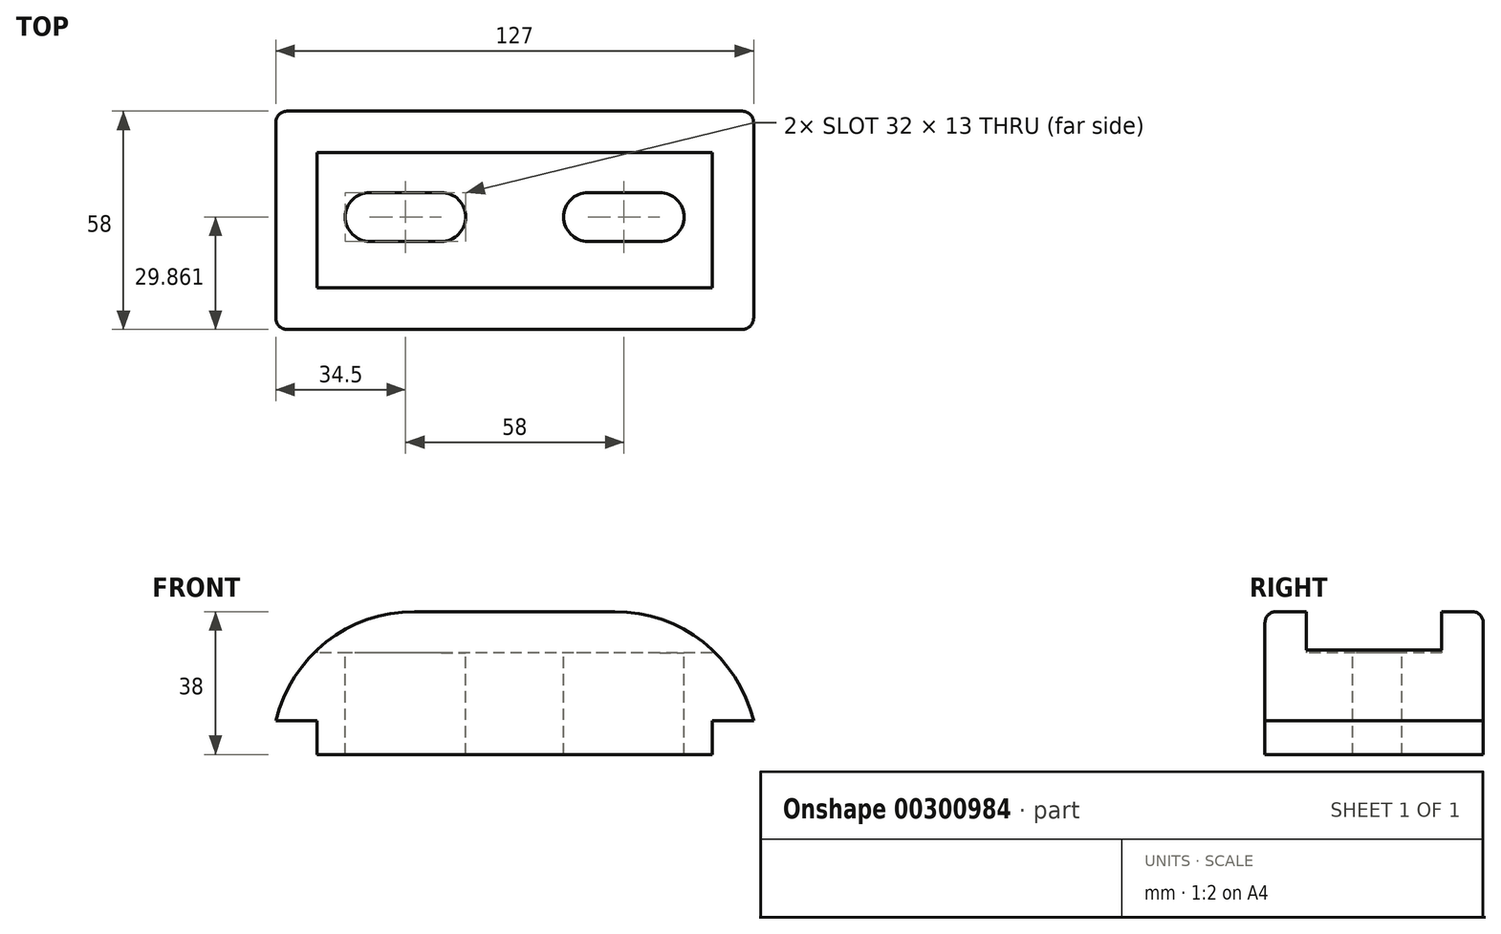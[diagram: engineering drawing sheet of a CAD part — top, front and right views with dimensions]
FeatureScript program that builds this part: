
annotation { "Feature Type Name" : "Feature", "Feature Type Description" : "" }
export const myFeature = defineFeature(function(context is Context, id is Id, definition is map)
    precondition{}
    {
        {
            var Q0;
            Q0=qCreatedBy(makeId("Front.planeOp"),FACE);
            var sketch = newSketch(context, id + "F0", { "sketchPlane" : qUnion([Q0])});
            skLineSegment(sketch, "E0", {"start": v(0, 0) * mm, "end": v(105, 0) * mm});
            skLineSegment(sketch, "E1", {"start": v(105, 0) * mm, "end": v(105, 9) * mm});
            skLineSegment(sketch, "E2", {"start": v(105, 9) * mm, "end": v(116, 9) * mm});
            skLineSegment(sketch, "E3", {"start": v(0, 0) * mm, "end": v(0, 9) * mm});
            skLineSegment(sketch, "E4", {"start": v(0, 9) * mm, "end": v(-11, 9) * mm});
            skLineSegment(sketch, "E5", {"start": v(25.92, 38) * mm, "end": v(79.08, 38) * mm});
            skArc(sketch, "E6", {"start": v(25.92, 38) * mm, "mid": v(2.45, 29.88) * mm, "end": v(-11, 9) * mm});
            skArc(sketch, "E7", {"start": v(116, 9) * mm, "mid": v(102.55, 29.88) * mm, "end": v(79.08, 38) * mm});
            skSolve(sketch);
        }
        {
            var Q0;
            Q0=makeQuery(id+"F0.imprint","IMPRINT",FACE,{"disambiguationData":[TD([[makeQuery(id+"F0.imprint","IMPRINT",EDGE,{"derivedFrom":sQuery(id+"F0.wireOp",EDGE,"E0")}),1.0]])]});
            extrude(context, id + "F1", {"entities" : qUnion([Q0]), "oppositeDirection" : true, "depth" : 58 * mm});
        }
        {
            var Q0;
            Q0=makeQuery(id+"F1.opExtrude","SWEPT_FACE",FACE,{"disambiguationData":[OSD([sQuery(id+"F0.wireOp",EDGE,"E0")])]});
            var sketch = newSketch(context, id + "F2", { "sketchPlane" : qUnion([Q0])});
            skLineSegment(sketch, "E8", {"start": v(105, -11) * mm, "end": v(0, -11) * mm});
            skLineSegment(sketch, "E9", {"start": v(105, -47) * mm, "end": v(0, -47) * mm});
            skLineSegment(sketch, "E10", {"start": v(105, -11) * mm, "end": v(105, -47) * mm});
            skLineSegment(sketch, "E11", {"start": v(0, -11) * mm, "end": v(0, -47) * mm});
            skSolve(sketch);
        }
        {
            var Q0;
            Q0=makeQuery(id+"F2.imprint","IMPRINT",FACE,{"disambiguationData":[TD([[makeQuery(id+"F2.imprint","IMPRINT",EDGE,{"derivedFrom":sQuery(id+"F2.wireOp",EDGE,"E8")}),1.0]])]});
            extrude(context, id + "F3", {"entities" : qUnion([Q0]), "operationType" : NewBodyOperationType.REMOVE, "oppositeDirection" : true, "depth" : 38 * mm, "hasSecondDirection" : true, "secondDirectionOppositeDirection" : true, "secondDirectionDepth" : 27 * mm});
        }
        {
            var Q0;
            Q0=makeQuery(id+"F1.opExtrude","CAP_EDGE",EDGE,{"disambiguationData":[OSD([sQuery(id+"F0.wireOp",EDGE,"E7")])],"isStart":false});
            var Q1;
            Q1=makeQuery(id+"F1.opExtrude","CAP_EDGE",EDGE,{"disambiguationData":[OSD([sQuery(id+"F0.wireOp",EDGE,"E5")])],"isStart":false});
            var Q2;
            Q2=makeQuery(id+"F1.opExtrude","CAP_EDGE",EDGE,{"disambiguationData":[OSD([sQuery(id+"F0.wireOp",EDGE,"E6")])],"isStart":false});
            fillet(context, id + "F4", {"entities" : qUnion([Q0, Q1, Q2]), "radius" : 3 * mm, "tangentPropagation" : true, "allowEdgeOverflow" : false});
        }
        {
            var Q0;
            Q0=makeQuery(id+"F1.opExtrude","CAP_EDGE",EDGE,{"disambiguationData":[OSD([sQuery(id+"F0.wireOp",EDGE,"E5")])],"isStart":true});
            var Q1;
            Q1=makeQuery(id+"F1.opExtrude","CAP_EDGE",EDGE,{"disambiguationData":[OSD([sQuery(id+"F0.wireOp",EDGE,"E6")])],"isStart":true});
            var Q2;
            Q2=makeQuery(id+"F1.opExtrude","CAP_EDGE",EDGE,{"disambiguationData":[OSD([sQuery(id+"F0.wireOp",EDGE,"E7")])],"isStart":true});
            fillet(context, id + "F5", {"entities" : qUnion([Q0, Q1, Q2]), "radius" : 3 * mm, "tangentPropagation" : true, "allowEdgeOverflow" : false});
        }
        {
            var Q0;
            Q0=makeQuery(id+"F3.boolean.opBoolean","COPY",FACE,{"derivedFrom":makeQuery(id+"F3.opExtrude","CAP_FACE",FACE,{"disambiguationData":[OSD([sQuery(id+"F2.wireOp",EDGE,"E8"),sQuery(id+"F2.wireOp",EDGE,"E9"),sQuery(id+"F2.wireOp",EDGE,"E10"),sQuery(id+"F2.wireOp",EDGE,"E11")])],"isStart":true})});
            var sketch = newSketch(context, id + "F6", { "sketchPlane" : qUnion([Q0])});
            skLineSegment(sketch, "E12", {"start": v(91, 29.86) * mm, "end": v(72, 29.86) * mm});
            skArc(sketch, "E13", {"start": v(91, 23.36) * mm, "mid": v(97.5, 29.86) * mm, "end": v(91, 36.36) * mm});
            skArc(sketch, "E14", {"start": v(72, 36.36) * mm, "mid": v(65.5, 29.86) * mm, "end": v(72, 23.36) * mm});
            skLineSegment(sketch, "E15", {"start": v(91, 36.36) * mm, "end": v(72, 36.36) * mm});
            skLineSegment(sketch, "E16", {"start": v(91, 23.36) * mm, "end": v(72, 23.36) * mm});
            skArc(sketch, "E17", {"start": v(14, 36.36) * mm, "mid": v(7.5, 29.86) * mm, "end": v(14, 23.36) * mm});
            skArc(sketch, "E18", {"start": v(33, 23.36) * mm, "mid": v(39.5, 29.86) * mm, "end": v(33, 36.36) * mm});
            skLineSegment(sketch, "E19", {"start": v(14, 23.36) * mm, "end": v(33, 23.36) * mm});
            skLineSegment(sketch, "E20", {"start": v(33, 36.36) * mm, "end": v(14, 36.36) * mm});
            skSolve(sketch);
        }
        {
            var Q0;
            Q0=makeQuery(id+"F6.imprint","IMPRINT",FACE,{"disambiguationData":[TD([[makeQuery(id+"F6.imprint","IMPRINT",EDGE,{"derivedFrom":sQuery(id+"F6.wireOp",EDGE,"E13")}),1.0]])]});
            var Q1;
            Q1=makeQuery(id+"F6.imprint","IMPRINT",FACE,{"disambiguationData":[TD([[makeQuery(id+"F6.imprint","IMPRINT",EDGE,{"derivedFrom":sQuery(id+"F6.wireOp",EDGE,"E17")}),1.0]])]});
            extrude(context, id + "F7", {"entities" : qUnion([Q0, Q1]), "operationType" : NewBodyOperationType.REMOVE, "oppositeDirection" : true, "depth" : 50 * mm});
        }
    });
